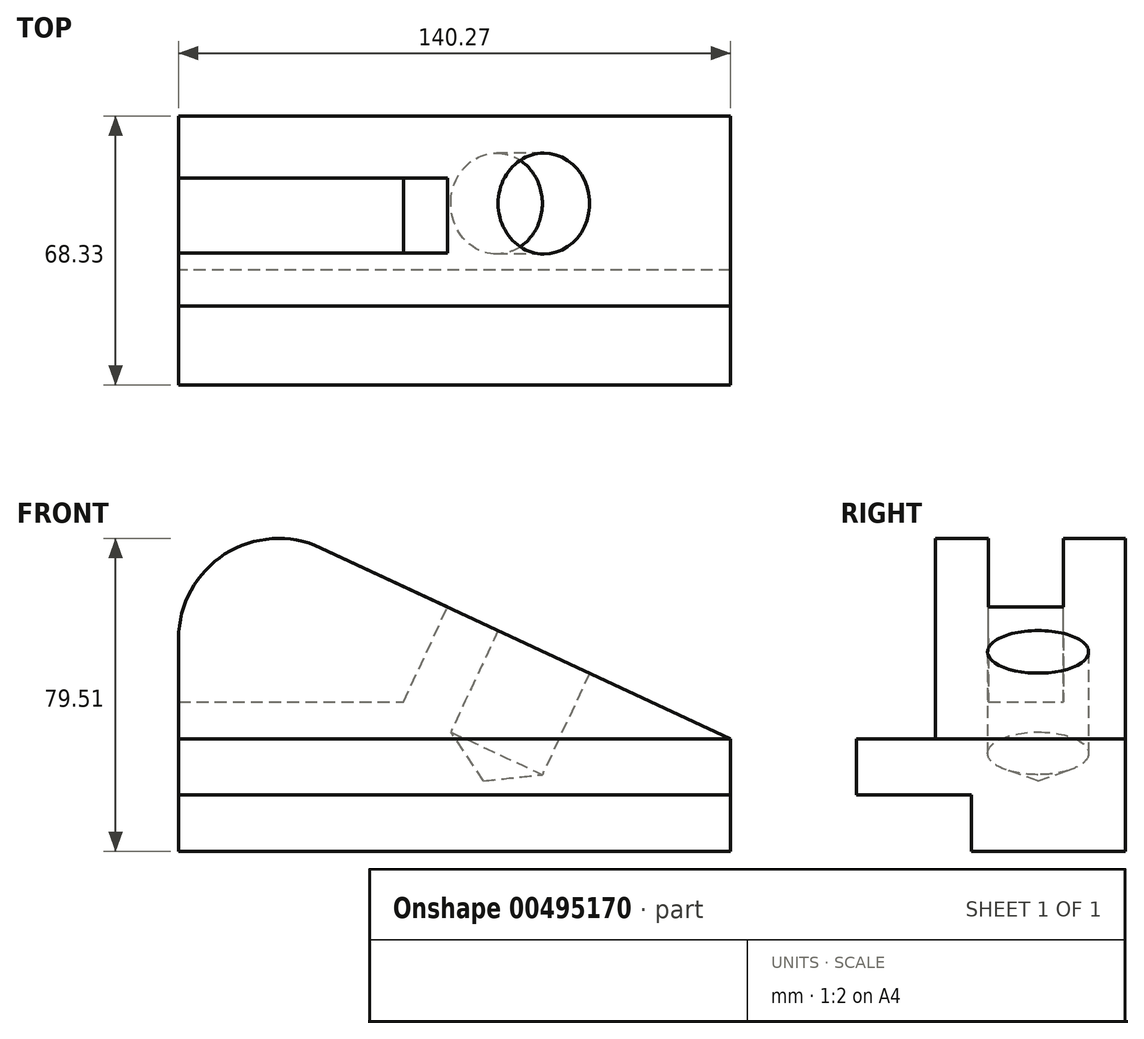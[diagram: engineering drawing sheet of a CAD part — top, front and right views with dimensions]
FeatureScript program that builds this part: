
annotation { "Feature Type Name" : "Feature", "Feature Type Description" : "" }
export const myFeature = defineFeature(function(context is Context, id is Id, definition is map)
    precondition{}
    {
        {
            var Q0;
            Q0=qCreatedBy(makeId("Front.planeOp"),FACE);
            var sketch = newSketch(context, id + "F0", { "sketchPlane" : qUnion([Q0])});
            skLineSegment(sketch, "E0", {"start": v(0, 0) * mm, "end": v(-140.27, 0) * mm});
            skLineSegment(sketch, "E1", {"start": v(-140.27, 0) * mm, "end": v(-140.27, 54.11) * mm});
            skLineSegment(sketch, "E2", {"start": v(0, 0) * mm, "end": v(0, 28.58) * mm});
            skLineSegment(sketch, "E3", {"start": v(0, 28.57) * mm, "end": v(-104.14, 77.13) * mm});
            skArc(sketch, "E4", {"start": v(-104.14, 77.13) * mm, "mid": v(-128.52, 75.54) * mm, "end": v(-140.27, 54.11) * mm});
            skSolve(sketch);
        }
        {
            var Q0;
            Q0 = qSketchRegion(id + "F0", true);
            extrude(context, id + "F1", {"entities" : qUnion([Q0]), "depth" : 68.33 * mm});
        }
        {
            var Q0;
            Q0=qCreatedBy(makeId("Right.planeOp"),FACE);
            var sketch = newSketch(context, id + "F2", { "sketchPlane" : qUnion([Q0])});
            skLineSegment(sketch, "E5.bottom", {"start": v(-39.12, 14.35) * mm, "end": v(-126.74, 14.35) * mm});
            skLineSegment(sketch, "E5.top", {"start": v(-39.12, -50.7) * mm, "end": v(-126.74, -50.7) * mm});
            skLineSegment(sketch, "E5.left", {"start": v(-39.12, 14.35) * mm, "end": v(-39.12, -50.7) * mm});
            skLineSegment(sketch, "E5.right", {"start": v(-126.74, 14.35) * mm, "end": v(-126.74, -50.7) * mm});
            skLineSegment(sketch, "E6.bottom", {"start": v(-118.73, 28.57) * mm, "end": v(-48.26, 28.57) * mm});
            skLineSegment(sketch, "E6.top", {"start": v(-118.73, 116.18) * mm, "end": v(-48.26, 116.18) * mm});
            skLineSegment(sketch, "E6.left", {"start": v(-118.73, 28.58) * mm, "end": v(-118.73, 116.18) * mm});
            skLineSegment(sketch, "E6.right", {"start": v(-48.26, 28.58) * mm, "end": v(-48.26, 116.18) * mm});
            skSolve(sketch);
        }
        {
            var Q0;
            Q0 = qSketchRegion(id + "F2", true);
            extrude(context, id + "F3", {"entities" : qUnion([Q0]), "operationType" : NewBodyOperationType.REMOVE, "endBound" : BoundingType.THROUGH_ALL, "oppositeDirection" : true, "depth" : 25.4 * mm});
        }
        {
            var Q0;
            Q0=makeQuery(id+"F1.opExtrude","CAP_FACE",FACE,{"disambiguationData":[OSD([sQuery(id+"F0.wireOp",EDGE,"E0"),sQuery(id+"F0.wireOp",EDGE,"E1"),sQuery(id+"F0.wireOp",EDGE,"E2"),sQuery(id+"F0.wireOp",EDGE,"E3"),sQuery(id+"F0.wireOp",EDGE,"E4")])],"isStart":true});
            cPlane(context, id + "F4", {"entities" : qUnion([Q0]), "cplaneType" : CPlaneType.OFFSET, "offset" : 22.22 * mm, "oppositeDirection" : true, "width" : 152.4 * mm, "height" : 152.4 * mm});
        }
        {
            var Q0;
            Q0=qCreatedBy(id+"F4.planeOp",FACE);
            var sketch = newSketch(context, id + "F5", { "sketchPlane" : qUnion([Q0])});
            skLineSegment(sketch, "E7", {"start": v(50.87, 73.77) * mm, "end": v(39.24, 68.35) * mm});
            skLineSegment(sketch, "E8", {"start": v(39.24, 68.35) * mm, "end": v(62.75, 17.94) * mm});
            skLineSegment(sketch, "E9", {"start": v(62.75, 17.94) * mm, "end": v(71.12, 30.35) * mm});
            skLineSegment(sketch, "E10", {"start": v(71.12, 30.35) * mm, "end": v(50.87, 73.77) * mm});
            skSolve(sketch);
        }
        {
            var Q0;
            Q0 = qSketchRegion(id + "F5", true);
            var Q1;
            Q1=sQuery(id+"F5.wireOp",EDGE,"E8");
            revolve(context, id + "F6", {"operationType" : NewBodyOperationType.REMOVE, "entities" : qUnion([Q0]), "axis" : qUnion([Q1]), "revolveType" : RevolveType.FULL, "oppositeDirection" : true});
        }
        {
            var Q0;
            Q0=makeQuery(id+"F1.opExtrude","CAP_FACE",FACE,{"disambiguationData":[OSD([sQuery(id+"F0.wireOp",EDGE,"E0"),sQuery(id+"F0.wireOp",EDGE,"E1"),sQuery(id+"F0.wireOp",EDGE,"E2"),sQuery(id+"F0.wireOp",EDGE,"E3"),sQuery(id+"F0.wireOp",EDGE,"E4")])],"isStart":true});
            cPlane(context, id + "F7", {"entities" : qUnion([Q0]), "cplaneType" : CPlaneType.OFFSET, "offset" : 15.75 * mm, "oppositeDirection" : true, "width" : 152.4 * mm, "height" : 152.4 * mm});
        }
        {
            var Q0;
            Q0=qCreatedBy(id+"F7.planeOp",FACE);
            var sketch = newSketch(context, id + "F8", { "sketchPlane" : qUnion([Q0])});
            skLineSegment(sketch, "E11", {"start": v(164.55, 123.75) * mm, "end": v(164.55, 38.05) * mm});
            skLineSegment(sketch, "E12", {"start": v(164.55, 38.05) * mm, "end": v(83.12, 38.05) * mm});
            skLineSegment(sketch, "E13", {"start": v(83.12, 38.05) * mm, "end": v(43.16, 123.75) * mm});
            skLineSegment(sketch, "E14", {"start": v(43.16, 123.75) * mm, "end": v(164.55, 123.75) * mm});
            skSolve(sketch);
        }
        {
            var Q0;
            Q0 = qSketchRegion(id + "F8", true);
            extrude(context, id + "F9", {"entities" : qUnion([Q0]), "operationType" : NewBodyOperationType.REMOVE, "oppositeDirection" : true, "depth" : 19.05 * mm});
        }
    });
